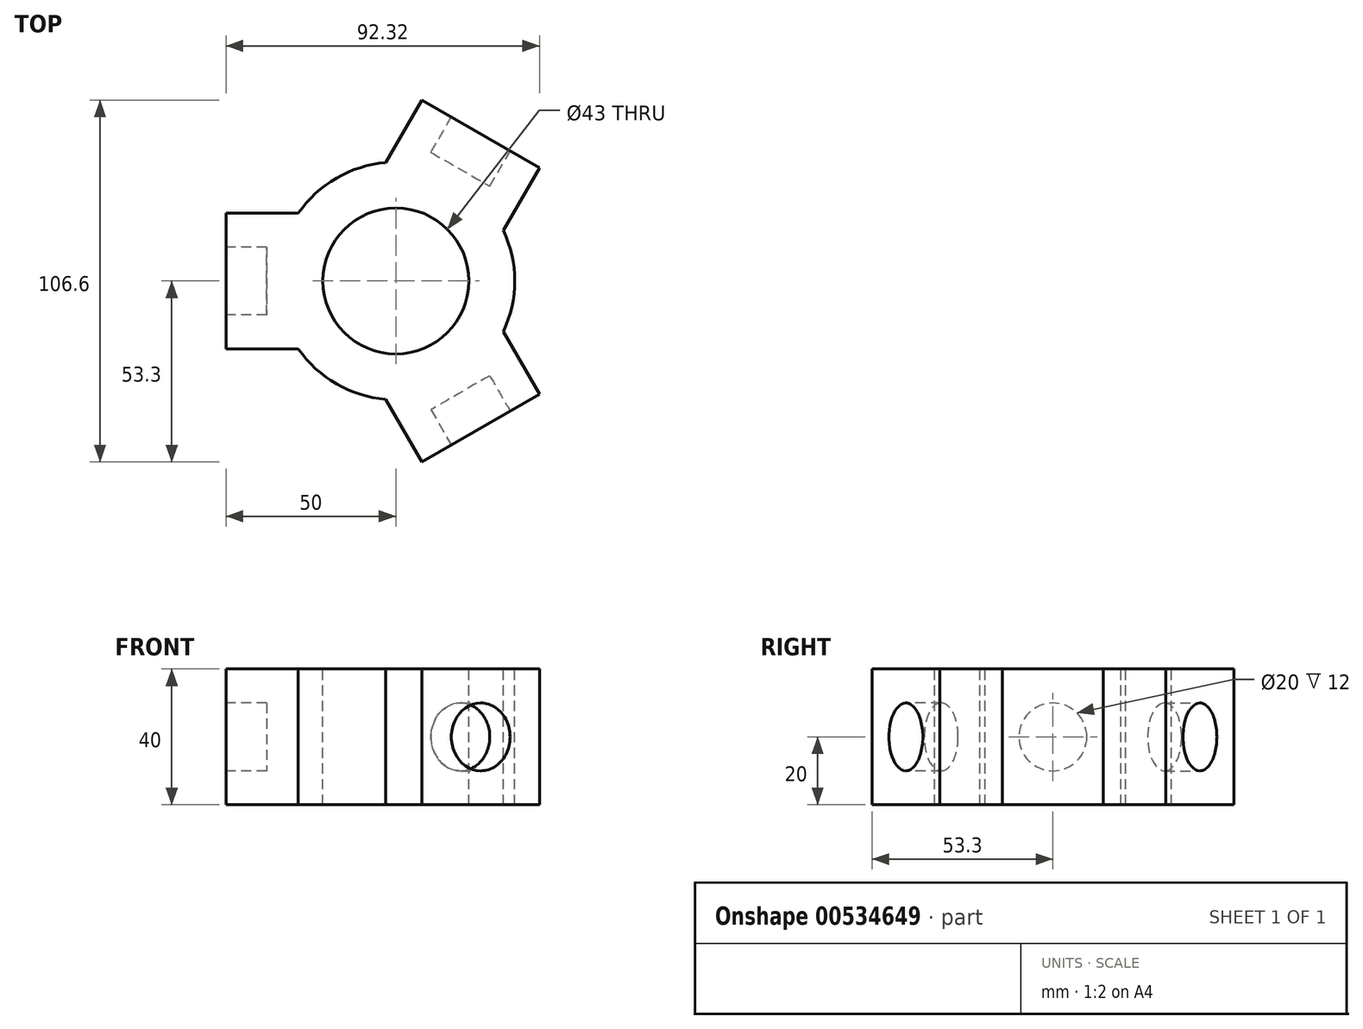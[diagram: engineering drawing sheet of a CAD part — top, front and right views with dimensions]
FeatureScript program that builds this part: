
annotation { "Feature Type Name" : "Feature", "Feature Type Description" : "" }
export const myFeature = defineFeature(function(context is Context, id is Id, definition is map)
    precondition{}
    {
        {
            var Q0;
            Q0=qCreatedBy(makeId("Top.planeOp"),FACE);
            var sketch = newSketch(context, id + "F0", { "sketchPlane" : qUnion([Q0])});
            skLineSegment(sketch, "E0", {"start": v(0, 0) * mm, "end": v(-50, 0) * mm, "construction": true});
            skLineSegment(sketch, "E1", {"start": v(0, 0) * mm, "end": v(25, 43.3) * mm, "construction": true});
            skLineSegment(sketch, "E2", {"start": v(0, 0) * mm, "end": v(25, -43.3) * mm, "construction": true});
            skArc(sketch, "E3", {"start": v(-2.96, 34.87) * mm, "mid": v(-17.5, 30.31) * mm, "end": v(-28.72, 20) * mm});
            skLineSegment(sketch, "E4", {"start": v(-28.72, 20) * mm, "end": v(-50, 20) * mm});
            skLineSegment(sketch, "E5", {"start": v(-50, 20) * mm, "end": v(-50, -20) * mm});
            skLineSegment(sketch, "E6", {"start": v(-50, -20) * mm, "end": v(-28.72, -20) * mm});
            skLineSegment(sketch, "E7", {"start": v(31.68, -14.87) * mm, "end": v(42.32, -33.3) * mm});
            skLineSegment(sketch, "E8", {"start": v(42.32, -33.3) * mm, "end": v(7.68, -53.3) * mm});
            skLineSegment(sketch, "E9", {"start": v(7.68, -53.3) * mm, "end": v(-2.96, -34.87) * mm});
            skLineSegment(sketch, "E10", {"start": v(-2.96, 34.87) * mm, "end": v(7.68, 53.3) * mm});
            skLineSegment(sketch, "E11", {"start": v(7.68, 53.3) * mm, "end": v(42.32, 33.3) * mm});
            skLineSegment(sketch, "E12", {"start": v(42.32, 33.3) * mm, "end": v(31.68, 14.87) * mm});
            skArc(sketch, "E13.trimOffspring", {"start": v(-28.72, -20) * mm, "mid": v(-17.5, -30.31) * mm, "end": v(-2.96, -34.87) * mm});
            skArc(sketch, "E14.trimOffspring", {"start": v(31.68, -14.87) * mm, "mid": v(35, 0) * mm, "end": v(31.68, 14.87) * mm});
            skCircle(sketch, "E15", {"center": v(0, 0) * mm, "radius": 21.5 * mm});
            skSolve(sketch);
        }
        {
            var Q0;
            Q0=makeQuery(id+"F0.imprint","IMPRINT",FACE,{"disambiguationData":[TD([[makeQuery(id+"F0.imprint","IMPRINT",EDGE,{"derivedFrom":sQuery(id+"F0.wireOp",EDGE,"E3")}),1.0]])]});
            var Q1;
            Q1=makeQuery(id+"F0.imprint","IMPRINT",FACE,{"disambiguationData":[TD([[makeQuery(id+"F0.imprint","IMPRINT",EDGE,{"derivedFrom":sQuery(id+"F0.wireOp",EDGE,"QRQUaUYH-IGAw-sJcJ-uih1-38r9zPpUmb9v")}),1.0]])]});
            var Q2;
            Q2=makeQuery(id+"F0.imprint","IMPRINT",FACE,{"disambiguationData":[TD([[makeQuery(id+"F0.imprint","IMPRINT",EDGE,{"derivedFrom":sQuery(id+"F0.wireOp",EDGE,"vKwHPlWU-oCB5-LQ7s-3ZyA-49lo3lMqQQpA")}),1.0]])]});
            var Q3;
            Q3=makeQuery(id+"F0.imprint","IMPRINT",FACE,{"disambiguationData":[TD([[makeQuery(id+"F0.imprint","IMPRINT",EDGE,{"derivedFrom":sQuery(id+"F0.wireOp",EDGE,"VVBaQmEC-vogH-ifRE-86vs-EFhndZVK8XVg")}),1.0]])]});
            extrude(context, id + "F1", {"entities" : qUnion([Q0, Q1, Q2, Q3]), "oppositeDirection" : true, "depth" : 40 * mm, "offsetDistance" : 25 * mm});
        }
        {
            var Q0;
            Q0=makeQuery(id+"F1.opExtrude","SWEPT_FACE",FACE,{"disambiguationData":[OSD([sQuery(id+"F0.wireOp",EDGE,"E5")])]});
            var sketch = newSketch(context, id + "F2", { "sketchPlane" : qUnion([Q0])});
            skCircle(sketch, "E16", {"center": v(0, -20) * mm, "radius": 10 * mm});
            skPoint(sketch, "E16.centerSnap0", {"position": v(0, -40) * mm});
            skPoint(sketch, "E16.centerSnap1", {"position": v(-20, -20) * mm});
            skSolve(sketch);
        }
        {
            var Q0;
            Q0=makeQuery(id+"F1.opExtrude","SWEPT_FACE",FACE,{"disambiguationData":[OSD([sQuery(id+"F0.wireOp",EDGE,"E8")])]});
            var sketch = newSketch(context, id + "F3", { "sketchPlane" : qUnion([Q0])});
            skCircle(sketch, "E17", {"center": v(0, -20) * mm, "radius": 10 * mm});
            skPoint(sketch, "E17.centerSnap0", {"position": v(20, -20) * mm});
            skSolve(sketch);
        }
        {
            var Q0;
            Q0=makeQuery(id+"F1.opExtrude","SWEPT_FACE",FACE,{"disambiguationData":[OSD([sQuery(id+"F0.wireOp",EDGE,"E11")])]});
            var sketch = newSketch(context, id + "F4", { "sketchPlane" : qUnion([Q0])});
            skCircle(sketch, "E18", {"center": v(0, -20) * mm, "radius": 10 * mm});
            skPoint(sketch, "E18.centerSnap0", {"position": v(20, -20) * mm});
            skSolve(sketch);
        }
        {
            var Q0;
            Q0 = qSketchRegion(id + "F2", true);
            extrude(context, id + "F5", {"entities" : qUnion([Q0]), "operationType" : NewBodyOperationType.REMOVE, "oppositeDirection" : true, "depth" : 12 * mm, "offsetDistance" : 25 * mm});
        }
        {
            var Q0;
            Q0 = qSketchRegion(id + "F3", true);
            extrude(context, id + "F6", {"entities" : qUnion([Q0]), "operationType" : NewBodyOperationType.REMOVE, "oppositeDirection" : true, "depth" : 12 * mm, "offsetDistance" : 25 * mm});
        }
        {
            var Q0;
            Q0 = qSketchRegion(id + "F4", true);
            extrude(context, id + "F7", {"entities" : qUnion([Q0]), "operationType" : NewBodyOperationType.REMOVE, "oppositeDirection" : true, "depth" : 12 * mm, "offsetDistance" : 25 * mm});
        }
    });
